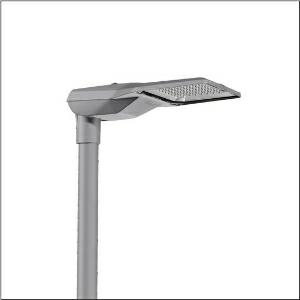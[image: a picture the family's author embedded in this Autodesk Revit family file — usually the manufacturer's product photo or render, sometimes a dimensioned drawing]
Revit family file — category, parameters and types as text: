
# Revit family: streetlight_sl_21_midi___pc-l_5xe3f43s08mb_b5db
name_source: partatom
category: Lighting Fixtures
units: mm (PartAtom-declared; Revit-internal decimal feet)

## family parameters
Cut with Voids When Loaded = No
Host = Face
Light Source = No
Part Type = Normal
Room Calculation Point = No
Round Connector Dimension = Use Diameter
Shared = No

## types (1)
- --- (1 x LED, 19200 lm, 147 W, 4000K)
    Apparent Load = 147 VA
    CIE Flux Codes = 38 78 98 100 100
    Color Rendering = 70
    Color Temperature = 4000K
    Default Elevation = 1800 mm
    Description = Streetlight SL 21 midi, mast luminaire, primary light control with lens, of PMMA, primary optical cover: cover, of toughened safety glass, transparent, light distribution: PC-L, light emission: direct distribution, primary light characteristic: asymmetric, left, installation type: side-entry, post-top, LED, High Power LED, rated luminous flux: 19.200lm, luminous efficacy: 131lm/W, light colour: 740, colour temperature: 4000K, control gear: D4i, control: overheat protection, constant luminous flux control, time-dependent luminous flux control, flexible luminous flux parameterisation, pre-setting: logarithmic dimming characteristic, mains connection: 230..240V, AC, 50/60Hz, start of lifetime: 147W, end of service life: 155W, reduction: 65W, luminaire housing, of diecast aluminium, powder-coated, Siteco® metallic grey (DB 702S), corrosivity category C5 mid according to DIN EN ISO 12944, please order mast flange separately, inclination adjustable: 0°, 5°, 10°, 15°, sealing non-destructively replaceable, multi-level sealing system, length: 644mm, width: 335mm, height: 110mm, mast flange for spigot size: 42mm (side-entry): 5XC10008XM4, 60/48mm (side-entry/post-top): 5XC10108XM2, 76/60mm (side-entry/post-top): 5XC10108XM1, mounting height: 4..8m, Smart Interface above, protection rating (complete): IP66, insulation class (complete): insulation class II (safety insulation), certification: CE, ENEC, ENEC+, VDE, impact resistance: IK10, permissible operating ambient temperature for outdoor applications: -40..+50°C, standard-compliant lighting for roads and squares, packaging unit: 1 piece

Light Distribution: PC-L
    Height = 111 mm
    Lamp = 1 x LED
    Lamp Light Flux = 19200 lm
    Lamp Power = 147 W
    Lamp count = 1
    Length = 644 mm
    Luminous efficacy = 131 lm/W
    Manufacturer = Siteco
    ModVariant = No
    Model = 5XE3F43S08MB
    Number of Poles = 1
    OnlyDefault = Yes
    Power Factor = 1
    Product Name = Streetlight SL 21 midi | PC-L
    Product group = mast luminaire | pylon top
    ProductGroupID = 6100
    Protection Class = Protection class II
    Protection Degree = IP 66
    RLX_Detail_Level = 1
    RLX_Emergency_Light_Flux = 0 lm
    RLX_Emergency_Type = 0
    RLX_Emergency_Type_DB = No
    RlxData = <blob elided: 29517 chars, md5=9859a7f1>
    Socket = socket
    Standby Power = 0 W
    System Light Flux = 19200 lm
    System Power = 147 W
    Type Comments = factory setting: luminous flux: 100 % | dim-lin: 254 | 750 mA
    Type Image = l_1004302.jpg
    URL = http://relux.com
    VarID = @adj_085725
    Voltage = 0 V
    Weight = 0.00 kg
    Width = 336 mm

## geometry (parser evidence)
native form markers: Blend x4, Sweep x10
no freeform markers — native parametric forms only
